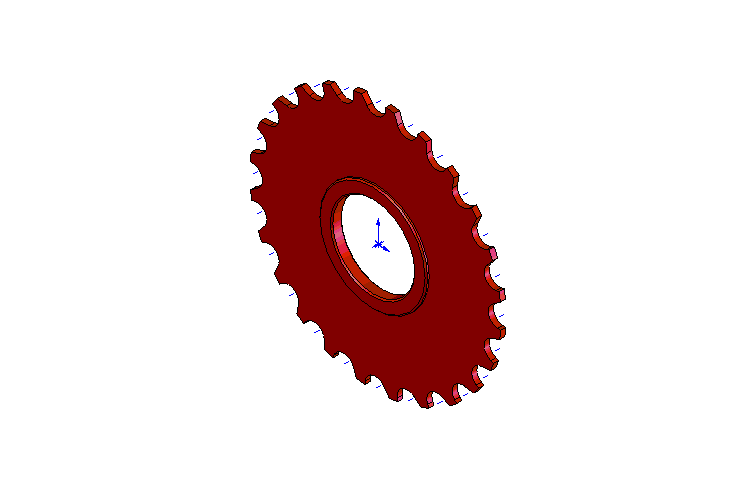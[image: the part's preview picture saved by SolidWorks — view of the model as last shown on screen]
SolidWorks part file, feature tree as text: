
SOLIDWORKS PART (.sldprt)
format: sldprt  version: not decoded by parser v0  size: 227,840 bytes
history: native  units: mm
features: sketch x4, plane x3, extrude x3, material x1, cut_extrude x1, pattern_circular x1, chamfer x1 (+10 scaffold rows collapsed)
feature tree (24):
  scaffold x10  (default folders/planes/origin — collapsed)
  material  "Matériau <non spécifié>"
  plane  "Plan de face"
  plane  "Plan de dessus"
  plane  "Plan de droite"
  sketch  "Esquisse1"  dims[D1=98.0mm]
  extrude  "Extrusion1"  Depth=2mm
  sketch  "Esquisse2"  dims[c1.D1=8.0mm c1.D3=4.0mm c2.D1=8.0mm c2.D3=4.0mm c2.D2=9.5mm c3.D3=4.0mm c3.D2=~2.039916mm c4.D2=35.0deg c4.D3=5.0mm]
  cut_extrude  "Enlèv. mat.-Extru.1"  [1 undecoded]
  pattern_circular  "Répétition circulaire1"  Count=24 Angle=15deg
  sketch  "Esquisse3"  dims[D1=42.0mm]
  extrude  "Extrusion2"  Depth=4.25mm
  sketch  "Esquisse4"  dims[D1=32.0mm]
  extrude  "Enlèv. mat.-Extru.2"  [1 undecoded]
  chamfer  "Chanfrein1"  Distance=0.5mm Angle=45deg
decode coverage: 8 of 10 modeling features carry decoded parameters
note: ~ marks probable driven/reference dimensions
note: 2 parameter values undecoded
note: suppression state not decoded; provenance and decode notes live in map.json
